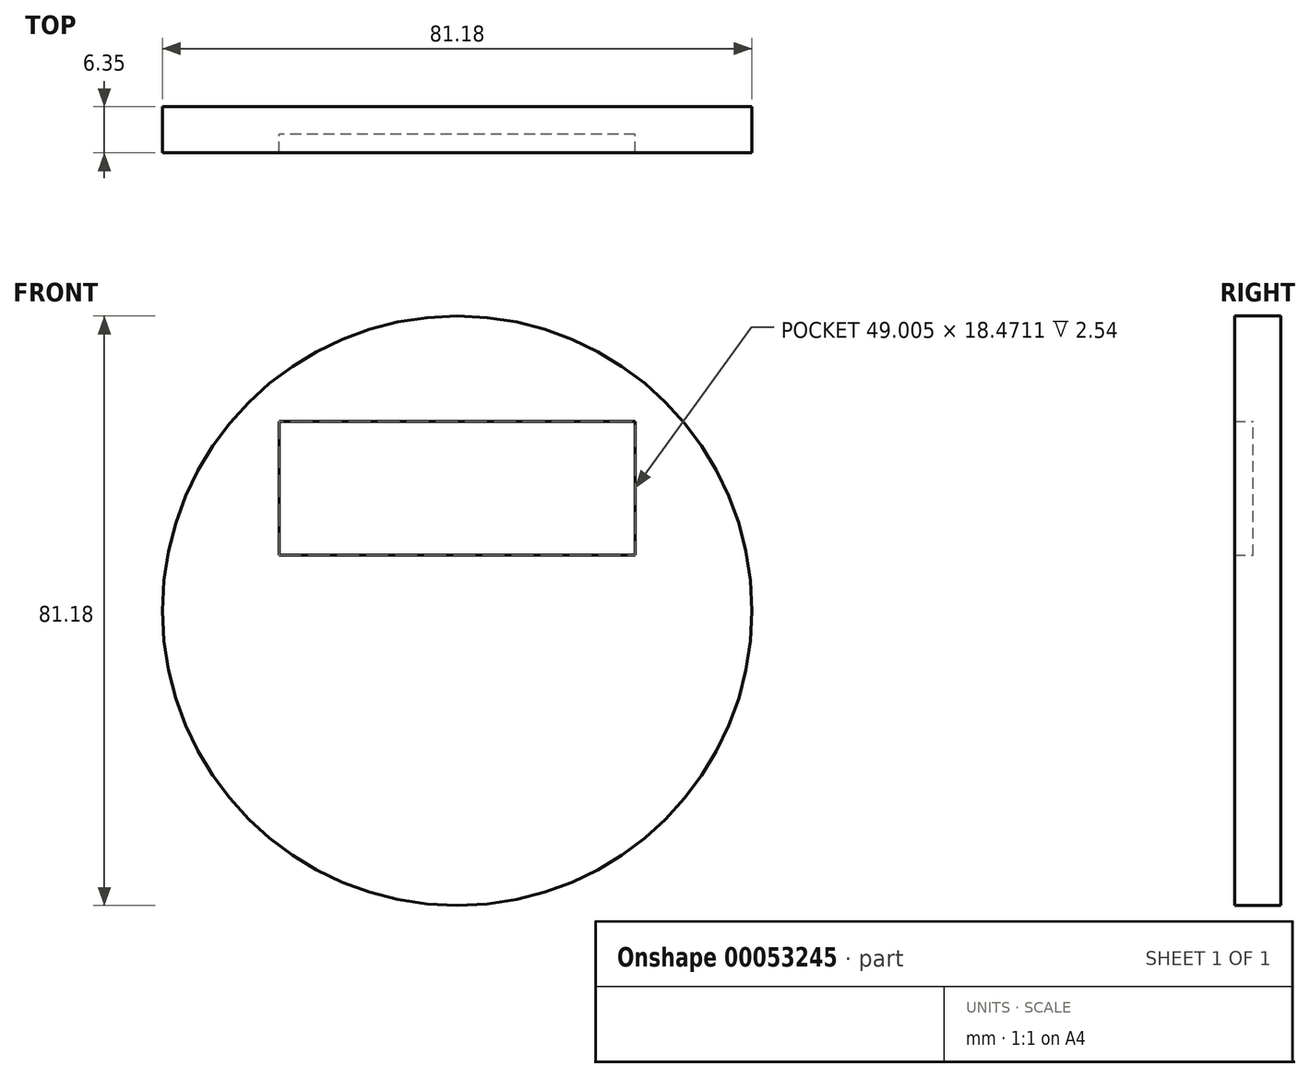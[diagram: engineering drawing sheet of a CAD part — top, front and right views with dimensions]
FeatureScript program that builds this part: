
annotation { "Feature Type Name" : "Feature", "Feature Type Description" : "" }
export const myFeature = defineFeature(function(context is Context, id is Id, definition is map)
    precondition{}
    {
        {
            var Q0;
            Q0=qCreatedBy(makeId("Front.planeOp"),FACE);
            var sketch = newSketch(context, id + "F0", { "sketchPlane" : qUnion([Q0])});
            skCircle(sketch, "E0", {"center": v(0, 0) * mm, "radius": 40.6 * mm});
            skLineSegment(sketch, "E1.rect.bottom", {"start": v(24.5, 7.63) * mm, "end": v(-24.5, 7.63) * mm});
            skLineSegment(sketch, "E1.rect.top", {"start": v(24.5, 26.1) * mm, "end": v(-24.5, 26.1) * mm});
            skLineSegment(sketch, "E1.rect.left", {"start": v(24.5, 7.63) * mm, "end": v(24.5, 26.1) * mm});
            skLineSegment(sketch, "E1.rect.right", {"start": v(-24.5, 7.63) * mm, "end": v(-24.5, 26.1) * mm});
            skPoint(sketch, "E1.rect.middle", {"position": v(0, 16.87) * mm});
            skSolve(sketch);
        }
        {
            var Q0;
            Q0=makeQuery(id+"F0.imprint","IMPRINT",FACE,{"disambiguationData":[TD([[makeQuery(id+"F0.imprint","IMPRINT",EDGE,{"derivedFrom":sQuery(id+"F0.wireOp",EDGE,"E0")}),1.0]])]});
            extrude(context, id + "F1", {"entities" : qUnion([Q0]), "depth" : 6.35 * mm});
        }
        {
            var Q0;
            Q0=makeQuery(id+"F0.imprint","IMPRINT",FACE,{"disambiguationData":[TD([[makeQuery(id+"F0.imprint","IMPRINT",EDGE,{"derivedFrom":sQuery(id+"F0.wireOp",EDGE,"E1.rect.bottom")}),-1.0]])]});
            extrude(context, id + "F2", {"entities" : qUnion([Q0]), "operationType" : NewBodyOperationType.ADD, "depth" : 3.8 * mm});
        }
    });
